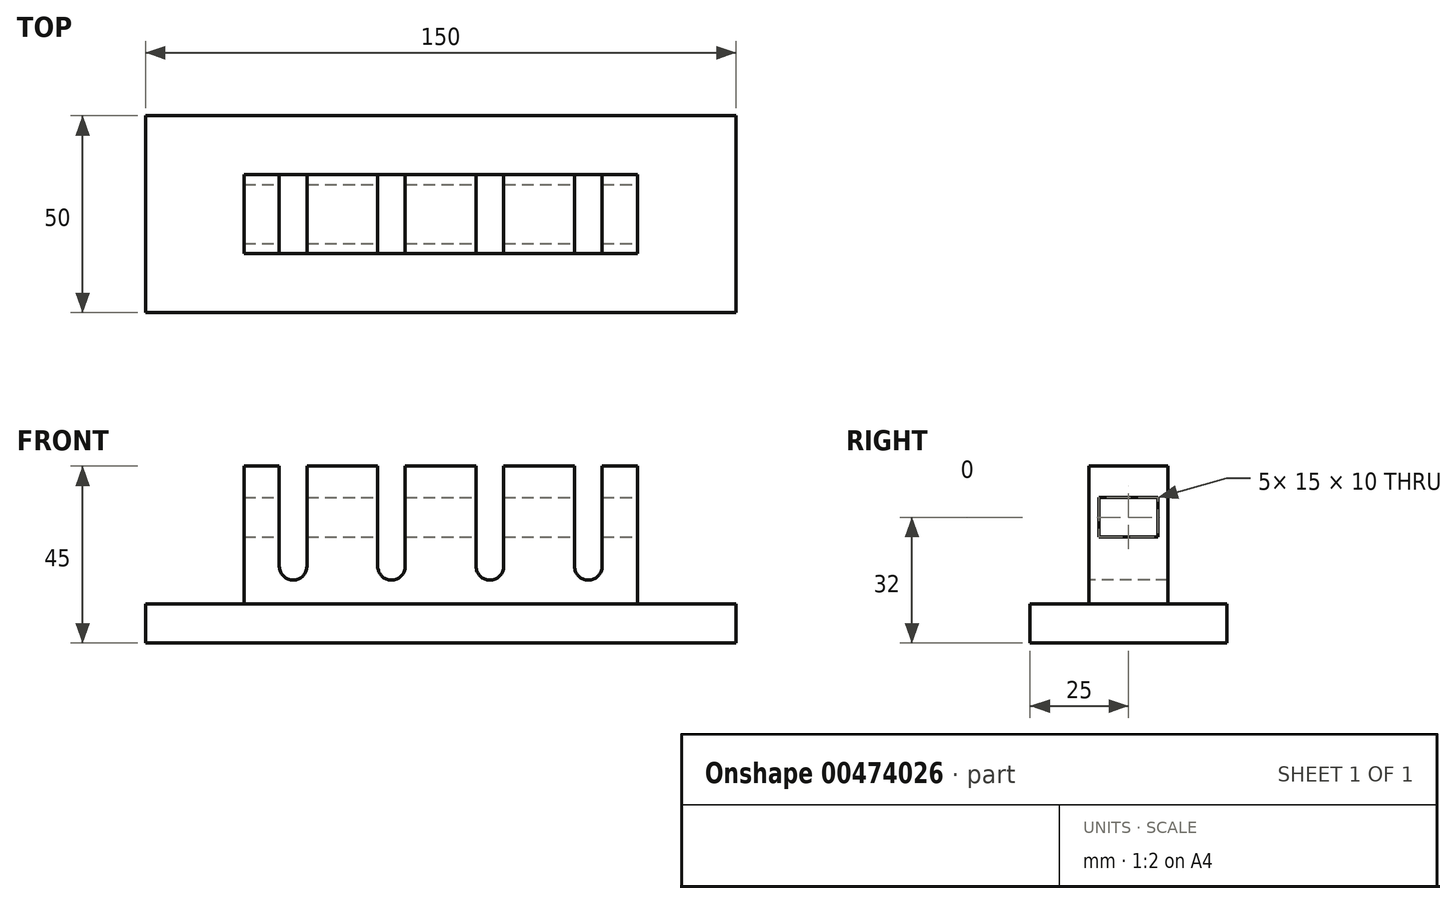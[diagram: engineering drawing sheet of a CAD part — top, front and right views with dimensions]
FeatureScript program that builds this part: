
annotation { "Feature Type Name" : "Feature", "Feature Type Description" : "" }
export const myFeature = defineFeature(function(context is Context, id is Id, definition is map)
    precondition{}
    {
        {
            var Q0;
            Q0=qCreatedBy(makeId("Top.planeOp"),FACE);
            var sketch = newSketch(context, id + "F0", { "sketchPlane" : qUnion([Q0])});
            skLineSegment(sketch, "E0.bottom", {"start": v(0, 0) * mm, "end": v(150, 0) * mm});
            skLineSegment(sketch, "E0.top", {"start": v(0, 50) * mm, "end": v(150, 50) * mm});
            skLineSegment(sketch, "E0.left", {"start": v(0, 0) * mm, "end": v(0, 50) * mm});
            skLineSegment(sketch, "E0.right", {"start": v(150, 0) * mm, "end": v(150, 50) * mm});
            skSolve(sketch);
        }
        {
            var Q0;
            Q0=makeQuery(id+"F0.imprint","IMPRINT",FACE,{"disambiguationData":[TD([[makeQuery(id+"F0.imprint","IMPRINT",EDGE,{"derivedFrom":sQuery(id+"F0.wireOp",EDGE,"E0.bottom")}),1.0]])]});
            extrude(context, id + "F1", {"entities" : qUnion([Q0]), "depth" : 10 * mm});
        }
        {
            var Q0;
            Q0=makeQuery(id+"F1.opExtrude","CAP_FACE",FACE,{"disambiguationData":[OSD([sQuery(id+"F0.wireOp",EDGE,"E0.bottom"),sQuery(id+"F0.wireOp",EDGE,"E0.top"),sQuery(id+"F0.wireOp",EDGE,"E0.left"),sQuery(id+"F0.wireOp",EDGE,"E0.right")])],"isStart":false});
            var sketch = newSketch(context, id + "F2", { "sketchPlane" : qUnion([Q0])});
            skLineSegment(sketch, "E1.bottom", {"start": v(25, 35) * mm, "end": v(125, 35) * mm});
            skLineSegment(sketch, "E1.top", {"start": v(25, 15) * mm, "end": v(125, 15) * mm});
            skLineSegment(sketch, "E1.left", {"start": v(25, 35) * mm, "end": v(25, 15) * mm});
            skLineSegment(sketch, "E1.right", {"start": v(125, 35) * mm, "end": v(125, 15) * mm});
            skSolve(sketch);
        }
        {
            var Q0;
            Q0=qSketchRegion(id+"F2",true);
            extrude(context, id + "F3", {"entities" : qUnion([Q0]), "operationType" : NewBodyOperationType.ADD, "depth" : 35 * mm});
        }
        {
            var Q0;
            Q0=makeQuery(id+"F3.opExtrude","SWEPT_FACE",FACE,{"disambiguationData":[OSD([sQuery(id+"F2.wireOp",EDGE,"E1.top")])]});
            var sketch = newSketch(context, id + "F4", { "sketchPlane" : qUnion([Q0])});
            skLineSegment(sketch, "E2", {"start": v(34, 45) * mm, "end": v(34, 19.5) * mm});
            skArc(sketch, "E3", {"start": v(34, 19.5) * mm, "mid": v(37.5, 16) * mm, "end": v(41, 19.5) * mm});
            skLineSegment(sketch, "E4", {"start": v(41, 19.5) * mm, "end": v(41, 45) * mm});
            skLineSegment(sketch, "E5", {"start": v(41, 45) * mm, "end": v(34, 45) * mm});
            skLineSegment(sketch, "E6", {"start": v(75, 45) * mm, "end": v(75, 10) * mm, "construction": true});
            skLineSegment(sketch, "E7.MirrorCS", {"start": v(116, 45) * mm, "end": v(116, 19.5) * mm});
            skArc(sketch, "E8.MirrorCS", {"start": v(116, 19.5) * mm, "mid": v(112.5, 16) * mm, "end": v(109, 19.5) * mm});
            skLineSegment(sketch, "E9.MirrorCS", {"start": v(109, 19.5) * mm, "end": v(109, 45) * mm});
            skLineSegment(sketch, "E10.MirrorCS", {"start": v(109, 45) * mm, "end": v(116, 45) * mm});
            skLineSegment(sketch, "E11", {"start": v(50, 45) * mm, "end": v(50, 10) * mm, "construction": true});
            skLineSegment(sketch, "E12.MirrorCS", {"start": v(59, 45) * mm, "end": v(66, 45) * mm});
            skLineSegment(sketch, "E13.MirrorCS", {"start": v(66, 45) * mm, "end": v(66, 19.5) * mm});
            skLineSegment(sketch, "E14.MirrorCS", {"start": v(59, 19.5) * mm, "end": v(59, 45) * mm});
            skArc(sketch, "E15.MirrorCS", {"start": v(66, 19.5) * mm, "mid": v(62.5, 16) * mm, "end": v(59, 19.5) * mm});
            skLineSegment(sketch, "E16.MirrorCS", {"start": v(91, 19.5) * mm, "end": v(91, 45) * mm});
            skLineSegment(sketch, "E17.MirrorCS", {"start": v(91, 45) * mm, "end": v(84, 45) * mm});
            skLineSegment(sketch, "E18.MirrorCS", {"start": v(84, 45) * mm, "end": v(84, 19.5) * mm});
            skArc(sketch, "E19.MirrorCS", {"start": v(84, 19.5) * mm, "mid": v(87.5, 16) * mm, "end": v(91, 19.5) * mm});
            skSolve(sketch);
        }
        {
            var Q0;
            Q0=qSketchRegion(id+"F4",true);
            extrude(context, id + "F5", {"entities" : qUnion([Q0]), "operationType" : NewBodyOperationType.REMOVE, "endBound" : BoundingType.THROUGH_ALL, "oppositeDirection" : true, "depth" : 25 * mm});
        }
        {
            var Q0;
            Q0=makeQuery(id+"F3.opExtrude","SWEPT_FACE",FACE,{"disambiguationData":[OSD([sQuery(id+"F2.wireOp",EDGE,"E1.right")])]});
            var sketch = newSketch(context, id + "F6", { "sketchPlane" : qUnion([Q0])});
            skLineSegment(sketch, "E20.bottom", {"start": v(17.5, 37) * mm, "end": v(32.5, 37) * mm});
            skLineSegment(sketch, "E20.top", {"start": v(17.5, 27) * mm, "end": v(32.5, 27) * mm});
            skLineSegment(sketch, "E20.left", {"start": v(17.5, 37) * mm, "end": v(17.5, 27) * mm});
            skLineSegment(sketch, "E20.right", {"start": v(32.5, 37) * mm, "end": v(32.5, 27) * mm});
            skSolve(sketch);
        }
        {
            var Q0;
            Q0=makeQuery(id+"F6.imprint","IMPRINT",FACE,{"disambiguationData":[TD([[makeQuery(id+"F6.imprint","IMPRINT",EDGE,{"derivedFrom":sQuery(id+"F6.wireOp",EDGE,"E20.bottom")}),-1.0]])]});
            extrude(context, id + "F7", {"entities" : qUnion([Q0]), "operationType" : NewBodyOperationType.REMOVE, "endBound" : BoundingType.THROUGH_ALL, "oppositeDirection" : true, "depth" : 25 * mm});
        }
    });
